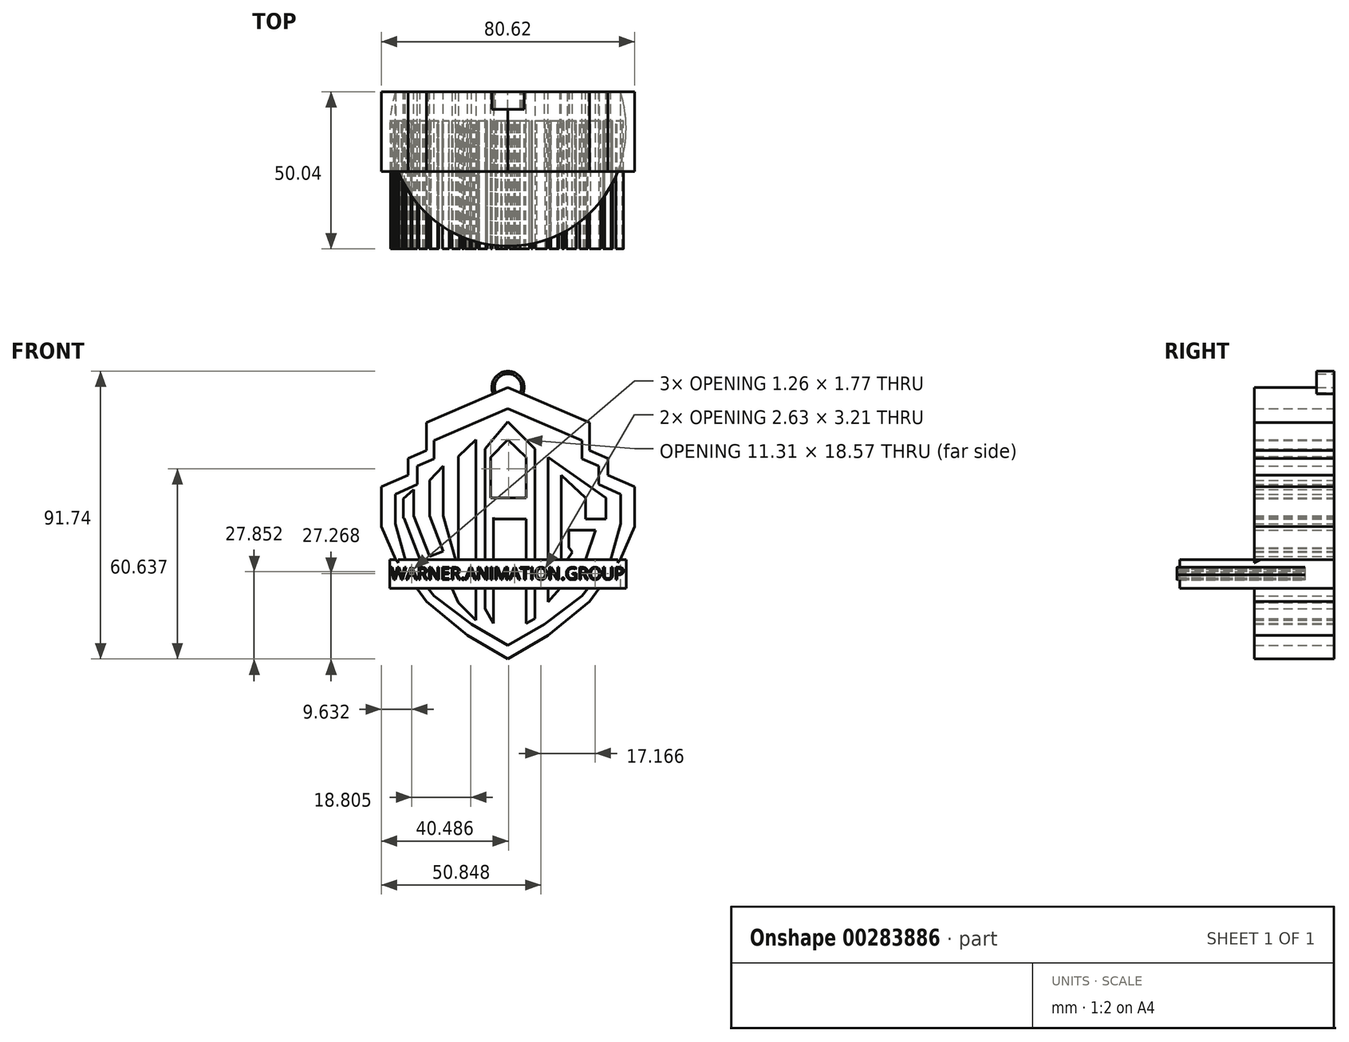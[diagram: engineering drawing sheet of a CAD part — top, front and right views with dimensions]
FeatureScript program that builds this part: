
annotation { "Feature Type Name" : "Feature", "Feature Type Description" : "" }
export const myFeature = defineFeature(function(context is Context, id is Id, definition is map)
    precondition{}
    {
        {
            var Q0;
            Q0=qCreatedBy(makeId("Front.planeOp"),FACE);
            var sketch = newSketch(context, id + "F0", { "sketchPlane" : qUnion([Q0])});
            skLineSegment(sketch, "E0", {"start": v(0, 48.24) * mm, "end": v(23.6, 38.04) * mm});
            skLineSegment(sketch, "E1", {"start": v(23.6, 38.04) * mm, "end": v(23.6, 32.2) * mm});
            skLineSegment(sketch, "E2", {"start": v(23.6, 32.2) * mm, "end": v(28.86, 29.88) * mm});
            skLineSegment(sketch, "E3", {"start": v(28.86, 29.88) * mm, "end": v(28.86, 24.05) * mm});
            skLineSegment(sketch, "E4", {"start": v(28.86, 24.05) * mm, "end": v(35.85, 20.84) * mm});
            skLineSegment(sketch, "E5", {"start": v(35.85, 20.84) * mm, "end": v(35.85, 11.51) * mm});
            skLineSegment(sketch, "E6", {"start": v(35.85, 11.51) * mm, "end": v(32.65, 0) * mm});
            skLineSegment(sketch, "E7", {"start": v(32.65, 0) * mm, "end": v(23.6, -11.51) * mm});
            skLineSegment(sketch, "E8", {"start": v(23.6, -11.51) * mm, "end": v(11.66, -20.55) * mm});
            skLineSegment(sketch, "E9", {"start": v(11.66, -20.55) * mm, "end": v(0, -27.25) * mm});
            skLineSegment(sketch, "E10.MirrorCS", {"start": v(-23.6, 38.04) * mm, "end": v(-23.6, 32.2) * mm});
            skLineSegment(sketch, "E11.MirrorCS", {"start": v(-23.6, 32.2) * mm, "end": v(-28.86, 29.88) * mm});
            skLineSegment(sketch, "E12.MirrorCS", {"start": v(-28.86, 29.88) * mm, "end": v(-28.86, 24.05) * mm});
            skLineSegment(sketch, "E13.MirrorCS", {"start": v(-28.86, 24.05) * mm, "end": v(-35.85, 20.84) * mm});
            skLineSegment(sketch, "E14.MirrorCS", {"start": v(0, 48.24) * mm, "end": v(-23.6, 38.04) * mm});
            skLineSegment(sketch, "E15.MirrorCS", {"start": v(-35.85, 20.84) * mm, "end": v(-35.85, 11.51) * mm});
            skLineSegment(sketch, "E16.MirrorCS", {"start": v(-23.6, -11.51) * mm, "end": v(-11.66, -20.55) * mm});
            skLineSegment(sketch, "E17.MirrorCS", {"start": v(-35.85, 11.51) * mm, "end": v(-32.65, 0) * mm});
            skLineSegment(sketch, "E18.MirrorCS", {"start": v(-32.65, 0) * mm, "end": v(-23.6, -11.51) * mm});
            skLineSegment(sketch, "E19.MirrorCS", {"start": v(-11.66, -20.55) * mm, "end": v(0, -27.25) * mm});
            skLineSegment(sketch, "E20", {"start": v(0, 54.94) * mm, "end": v(25.93, 43.74) * mm});
            skLineSegment(sketch, "E21", {"start": v(25.93, 43.74) * mm, "end": v(25.93, 34.83) * mm});
            skLineSegment(sketch, "E22", {"start": v(25.93, 34.83) * mm, "end": v(31.77, 32.3) * mm});
            skLineSegment(sketch, "E23", {"start": v(31.77, 32.3) * mm, "end": v(31.77, 26.96) * mm});
            skLineSegment(sketch, "E24", {"start": v(31.77, 26.96) * mm, "end": v(40.3, 23.27) * mm});
            skLineSegment(sketch, "E25", {"start": v(40.3, 23.27) * mm, "end": v(40.3, 10.64) * mm});
            skLineSegment(sketch, "E26", {"start": v(40.3, 10.64) * mm, "end": v(35.7, 0) * mm});
            skLineSegment(sketch, "E27", {"start": v(35.7, 0) * mm, "end": v(25.93, -13.26) * mm});
            skLineSegment(sketch, "E28", {"start": v(25.93, -13.26) * mm, "end": v(12.82, -24.05) * mm});
            skLineSegment(sketch, "E29", {"start": v(12.82, -24.05) * mm, "end": v(0, -31.63) * mm});
            skLineSegment(sketch, "E30.MirrorCS", {"start": v(0, 54.94) * mm, "end": v(-25.93, 43.74) * mm});
            skLineSegment(sketch, "E31.MirrorCS", {"start": v(-25.93, 43.74) * mm, "end": v(-25.93, 34.83) * mm});
            skLineSegment(sketch, "E32.MirrorCS", {"start": v(-31.77, 26.96) * mm, "end": v(-40.3, 23.27) * mm});
            skLineSegment(sketch, "E33.MirrorCS", {"start": v(-40.3, 23.27) * mm, "end": v(-40.3, 10.64) * mm});
            skLineSegment(sketch, "E34.MirrorCS", {"start": v(-40.3, 10.64) * mm, "end": v(-35.7, 0) * mm});
            skLineSegment(sketch, "E35.MirrorCS", {"start": v(-35.7, 0) * mm, "end": v(-25.93, -13.26) * mm});
            skLineSegment(sketch, "E36.MirrorCS", {"start": v(-25.93, -13.26) * mm, "end": v(-12.82, -24.05) * mm});
            skLineSegment(sketch, "E37.MirrorCS", {"start": v(-12.82, -24.05) * mm, "end": v(0, -31.63) * mm});
            skLineSegment(sketch, "E38.MirrorCS", {"start": v(-25.93, 34.83) * mm, "end": v(-31.77, 32.3) * mm});
            skLineSegment(sketch, "E39.MirrorCS", {"start": v(-31.77, 32.3) * mm, "end": v(-31.77, 26.96) * mm});
            skLineSegment(sketch, "E40", {"start": v(-33.35, 19.45) * mm, "end": v(-33.35, 13.27) * mm});
            skLineSegment(sketch, "E41", {"start": v(-33.08, 13.27) * mm, "end": v(-27.97, 0) * mm});
            skLineSegment(sketch, "E42", {"start": v(-27.97, 0) * mm, "end": v(-23.93, -5.3) * mm});
            skLineSegment(sketch, "E43", {"start": v(-23.93, -5.3) * mm, "end": v(-20.63, -2.79) * mm});
            skLineSegment(sketch, "E44", {"start": v(-20.63, -2.79) * mm, "end": v(-15.86, -13.64) * mm});
            skLineSegment(sketch, "E45", {"start": v(-15.86, -13.64) * mm, "end": v(-10.2, -19.3) * mm});
            skLineSegment(sketch, "E46", {"start": v(-10.2, -18.76) * mm, "end": v(-10.2, 38.3) * mm});
            skLineSegment(sketch, "E47", {"start": v(-10.2, 38.3) * mm, "end": v(-15.86, 32.9) * mm});
            skLineSegment(sketch, "E48", {"start": v(-15.86, 32.9) * mm, "end": v(-15.86, -2.79) * mm});
            skLineSegment(sketch, "E49", {"start": v(-15.86, -2.79) * mm, "end": v(-20.63, 14.07) * mm});
            skLineSegment(sketch, "E50", {"start": v(-20.63, 14.07) * mm, "end": v(-20.63, 29.95) * mm});
            skLineSegment(sketch, "E51", {"start": v(-20.63, 29.95) * mm, "end": v(-25, 25.37) * mm});
            skLineSegment(sketch, "E52", {"start": v(-25, 25.37) * mm, "end": v(-25, 14.07) * mm});
            skLineSegment(sketch, "E53", {"start": v(-25, 14.07) * mm, "end": v(-20.63, 2.77) * mm});
            skLineSegment(sketch, "E54", {"start": v(-20.63, 2.77) * mm, "end": v(-25, 1.08) * mm});
            skLineSegment(sketch, "E55", {"start": v(-25, 1.08) * mm, "end": v(-30.04, 14.07) * mm});
            skLineSegment(sketch, "E56", {"start": v(-30.04, 14.07) * mm, "end": v(-30.04, 22.41) * mm});
            skLineSegment(sketch, "E57", {"start": v(-30.04, 22.41) * mm, "end": v(-33.35, 19.45) * mm});
            skLineSegment(sketch, "E58", {"start": v(0, 43.94) * mm, "end": v(8.56, 35.33) * mm});
            skLineSegment(sketch, "E59", {"start": v(8.56, 35.33) * mm, "end": v(8.56, -18.76) * mm});
            skLineSegment(sketch, "E60", {"start": v(8.56, -18.76) * mm, "end": v(5.83, -20.33) * mm});
            skPoint(sketch, "E60.endSnap0", {"position": v(5.83, -23.9) * mm});
            skLineSegment(sketch, "E61", {"start": v(5.83, -20.33) * mm, "end": v(5.83, 13) * mm});
            skLineSegment(sketch, "E62", {"start": v(5.83, 13) * mm, "end": v(-4.36, 13) * mm});
            skLineSegment(sketch, "E63", {"start": v(-4.63, 13.53) * mm, "end": v(-4.63, -20.33) * mm});
            skLineSegment(sketch, "E64", {"start": v(-4.63, -20.33) * mm, "end": v(-7.34, -15.61) * mm});
            skLineSegment(sketch, "E65", {"start": v(-7.34, -15.61) * mm, "end": v(-7.34, 35.33) * mm});
            skLineSegment(sketch, "E66", {"start": v(-7.34, 35.33) * mm, "end": v(0, 43.94) * mm});
            skLineSegment(sketch, "E67", {"start": v(0, 19.72) * mm, "end": v(5.83, 19.72) * mm});
            skLineSegment(sketch, "E68", {"start": v(5.83, 19.72) * mm, "end": v(5.83, 32.64) * mm});
            skLineSegment(sketch, "E69", {"start": v(5.83, 32.64) * mm, "end": v(0, 38.3) * mm});
            skLineSegment(sketch, "E70", {"start": v(0, 38.3) * mm, "end": v(-5.48, 32.64) * mm});
            skLineSegment(sketch, "E71", {"start": v(-5.48, 32.64) * mm, "end": v(-5.48, 19.72) * mm});
            skLineSegment(sketch, "E72", {"start": v(-5.48, 19.72) * mm, "end": v(0, 19.72) * mm});
            skLineSegment(sketch, "E73", {"start": v(12.82, 32.64) * mm, "end": v(12.82, -13.37) * mm});
            skLineSegment(sketch, "E74", {"start": v(12.82, -13.37) * mm, "end": v(24.7, 0) * mm});
            skLineSegment(sketch, "E75", {"start": v(24.7, 0) * mm, "end": v(27.93, 9.5) * mm});
            skLineSegment(sketch, "E76", {"start": v(27.93, 9.5) * mm, "end": v(19.32, 9.5) * mm});
            skLineSegment(sketch, "E77", {"start": v(19.32, 9.5) * mm, "end": v(19.32, 3.85) * mm});
            skLineSegment(sketch, "E78", {"start": v(19.6, 3.58) * mm, "end": v(20.47, 2.41) * mm});
            skLineSegment(sketch, "E79", {"start": v(20.47, 2.41) * mm, "end": v(16.9, -2.88) * mm});
            skLineSegment(sketch, "E80", {"start": v(16.9, -2.88) * mm, "end": v(16.9, 26.99) * mm});
            skLineSegment(sketch, "E81", {"start": v(16.9, 26.99) * mm, "end": v(24.7, 19.72) * mm});
            skLineSegment(sketch, "E82", {"start": v(24.7, 19.72) * mm, "end": v(24.7, 13) * mm});
            skLineSegment(sketch, "E83", {"start": v(24.7, 13) * mm, "end": v(31.16, 13) * mm});
            skLineSegment(sketch, "E84", {"start": v(31.16, 13) * mm, "end": v(31.16, 19.72) * mm});
            skLineSegment(sketch, "E85", {"start": v(31.16, 19.72) * mm, "end": v(12.82, 32.64) * mm});
            skLineSegment(sketch, "E86", {"start": v(-10.2, -18.76) * mm, "end": v(-10.2, -19.3) * mm});
            skLineSegment(sketch, "E87", {"start": v(19.6, 3.58) * mm, "end": v(19.33, 3.58) * mm});
            skLineSegment(sketch, "E88", {"start": v(19.33, 3.58) * mm, "end": v(19.32, 3.85) * mm});
            skLineSegment(sketch, "E89", {"start": v(-4.36, 13) * mm, "end": v(-4.63, 13.53) * mm});
            skLineSegment(sketch, "E90", {"start": v(-33.35, 13.27) * mm, "end": v(-33.08, 13.27) * mm});
            skLineSegment(sketch, "E91", {"start": v(19.6, 3.58) * mm, "end": v(19.32, 3.85) * mm});
            skSolve(sketch);
        }
        {
            var Q0;
            Q0 = qSketchRegion(id + "F0", true);
            var Q1;
            Q1=makeQuery(id+"F0.imprint","IMPRINT",FACE,{"disambiguationData":[TD([[makeQuery(id+"F0.imprint","IMPRINT",EDGE,{"derivedFrom":sQuery(id+"F0.wireOp",EDGE,"E73")}),1.0]])]});
            var Q2;
            Q2=makeQuery(id+"F0.imprint","IMPRINT",FACE,{"disambiguationData":[TD([[makeQuery(id+"F0.imprint","IMPRINT",EDGE,{"derivedFrom":sQuery(id+"F0.wireOp",EDGE,"E58")}),-1.0]])]});
            var Q3;
            Q3=makeQuery(id+"F0.imprint","IMPRINT",FACE,{"disambiguationData":[TD([[makeQuery(id+"F0.imprint","IMPRINT",EDGE,{"derivedFrom":sQuery(id+"F0.wireOp",EDGE,"E40")}),1.0]])]});
            extrude(context, id + "F1", {"entities" : qUnion([Q0, Q1, Q2, Q3]), "depth" : 25.4 * mm});
        }
        {
            var Q0;
            Q0=qCreatedBy(makeId("Top.planeOp"),FACE);
            var sketch = newSketch(context, id + "F2", { "sketchPlane" : qUnion([Q0])});
            skArc(sketch, "E92", {"start": v(-35.82, 0) * mm, "mid": v(0, -49.18) * mm, "end": v(35.82, 0) * mm});
            skArc(sketch, "E93", {"start": v(-33.2, 0) * mm, "mid": v(0, -46.7) * mm, "end": v(33.2, 0) * mm});
            skLineSegment(sketch, "E94", {"start": v(-35.82, 0) * mm, "end": v(35.82, 0) * mm});
            skSolve(sketch);
        }
        {
            var Q0;
            Q0 = qSketchRegion(id + "F2", true);
            extrude(context, id + "F3", {"entities" : qUnion([Q0]), "operationType" : NewBodyOperationType.ADD, "oppositeDirection" : true, "depth" : 9.14 * mm});
        }
        {
            var Q0;
            Q0=qCreatedBy(makeId("Front.planeOp"),FACE);
            var sketch = newSketch(context, id + "F4", { "sketchPlane" : qUnion([Q0])});
            skText(sketch, "E95", { "text": "WARNER.ANIMATION.GROUP", "fontName": "OpenSans-Regular.ttf"});
            const initialGuessF4  = {"E95": [-0.03746, -0.00631, 1, 0, 0.00393]};
            skSetInitialGuess(sketch, initialGuessF4);
            skSolve(sketch);
        }
        {
            var Q0;
            Q0 = qSketchRegion(id + "F4", true);
            extrude(context, id + "F5", {"entities" : qUnion([Q0]), "depth" : 50.04 * mm, "hasSecondDirection" : true, "secondDirectionOppositeDirection" : false, "secondDirectionDepth" : 9.3 * mm});
        }
        {
            var Q0;
            Q0=qCreatedBy(makeId("Front.planeOp"),FACE);
            var sketch = newSketch(context, id + "F6", { "sketchPlane" : qUnion([Q0])});
            skCircle(sketch, "E96", {"center": v(0, 54.97) * mm, "radius": 5.14 * mm});
            skCircle(sketch, "E97", {"center": v(0, 54.97) * mm, "radius": 4.3 * mm});
            skSolve(sketch);
        }
        {
            var Q0;
            Q0 = qSketchRegion(id + "F6", true);
            extrude(context, id + "F7", {"entities" : qUnion([Q0]), "operationType" : NewBodyOperationType.ADD, "depth" : 5.56 * mm});
        }
    });
